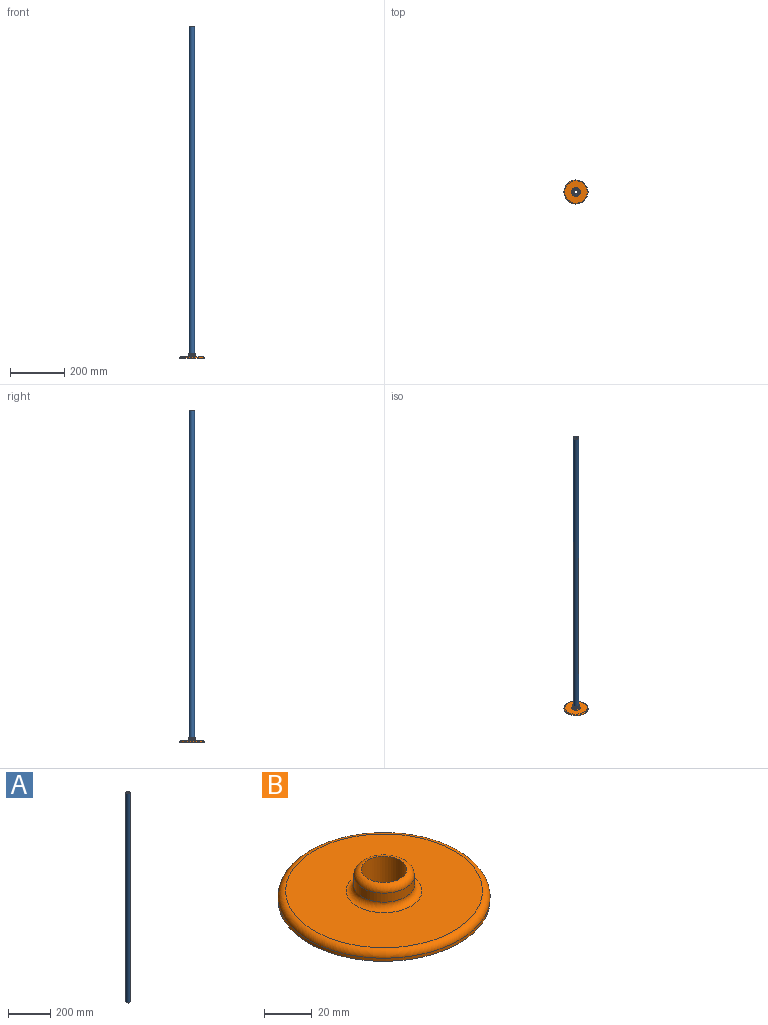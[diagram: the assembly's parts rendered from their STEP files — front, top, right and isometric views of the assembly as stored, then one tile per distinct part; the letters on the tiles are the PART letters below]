
ASSEMBLY  parts=2 mates=1
PART A: 4 faces, bbox 19.1x19.1x1219.2 mm
  f0: cylinder r=6.99mm len=1219.2mm, axis (0,0,-1), area 53508.3mm2, adj f2,f3
  f1: cylinder r=9.53mm len=1219.2mm, axis (0,0,-1), area 72965.9mm2, adj f2,f3
  f2: plane 19.05x19.05mm, normal (0,0,1), area 131.7mm2, adj f0,f1
  f3: plane 19.05x19.05mm, normal (0,0,-1), area 131.7mm2, adj f0,f1
PART B: 8 faces, bbox 96.2x96.2x15.7 mm
  f0: cylinder r=44.45mm len=88.9mm, axis (0,0,-1), area 443.4mm2, adj f2,f7
  f1: plane 82.55x82.55mm, normal (0,0,1), area 4560.4mm2, adj f5,f7
  f2: plane 88.9x88.9mm, normal (0,0,-1), area 5922.1mm2, adj f0,f3
  f3: cylinder r=9.53mm len=19.05mm, axis (0,0,1), area 942.5mm2, adj f2,f6
  f4: cylinder r=12.7mm len=25.4mm, axis (0,0,-1), area 369.9mm2, adj f5,f6
  f5: torus R=15.88mm, axis (0,0,1), area 434.1mm2, adj f1,f4
  f6: torus R=9.53mm, axis (0,0,1), area 361.8mm2, adj f3,f4
  f7: torus R=41.27mm, axis (0,0,1), area 1356.7mm2, adj f0,f1
PLACE A t=(-15.07,61.62,5.94)mm
PLACE B t=(-15.07,61.62,0)mm
MATE cylindrical A.f0 <-> B.f0  axis (0,0,-1) through (-15.07,61.62,615.54)mm
